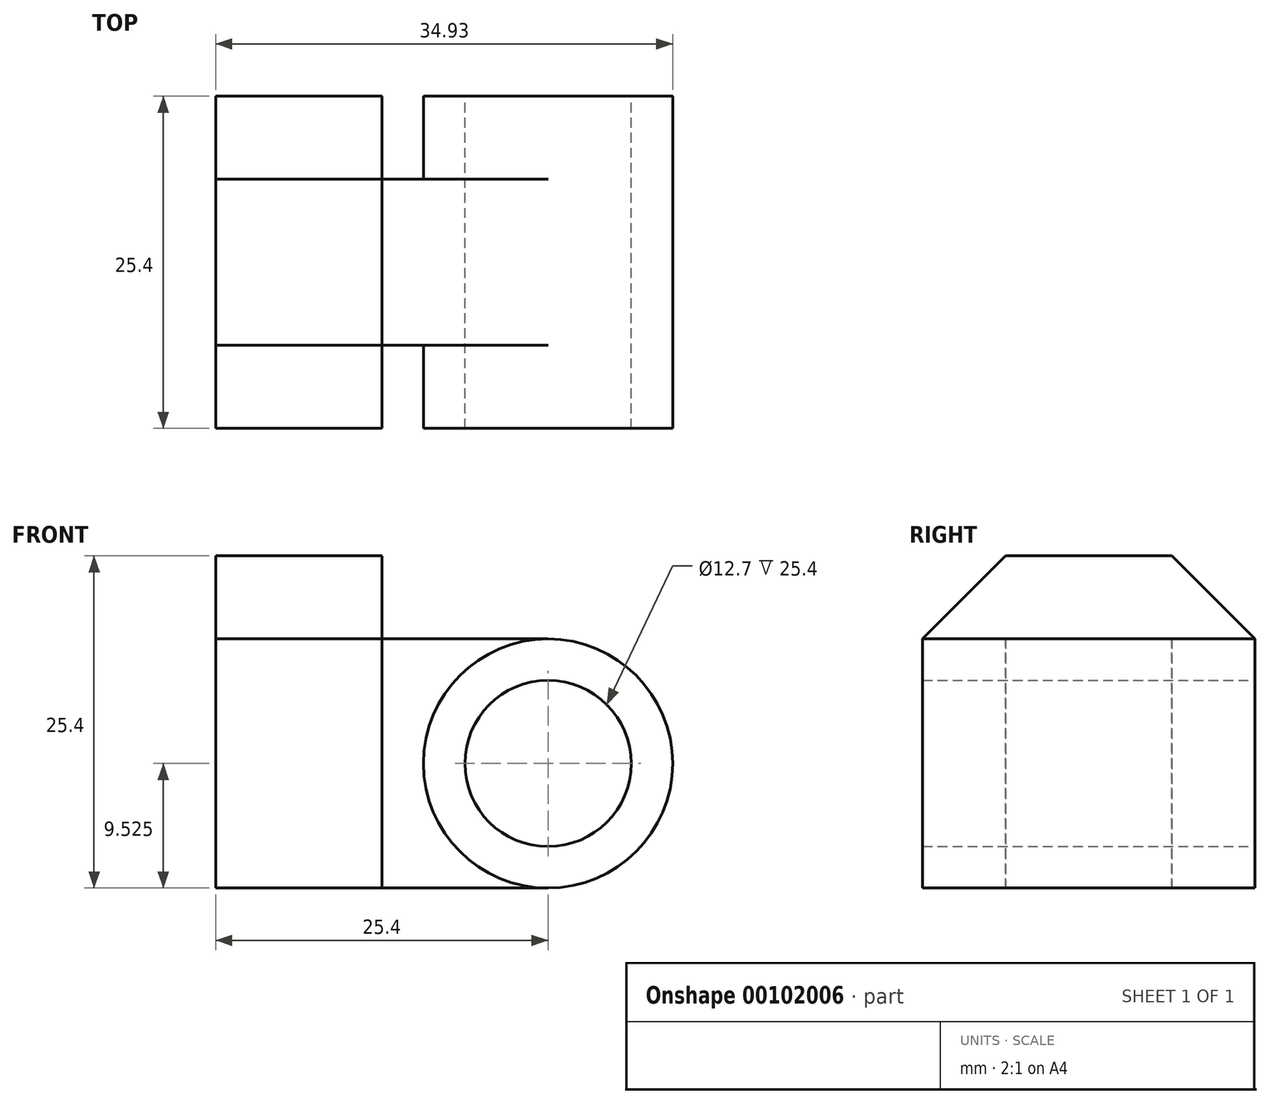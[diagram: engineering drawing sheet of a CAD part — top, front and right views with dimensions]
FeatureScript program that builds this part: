
annotation { "Feature Type Name" : "Feature", "Feature Type Description" : "" }
export const myFeature = defineFeature(function(context is Context, id is Id, definition is map)
    precondition{}
    {
        {
            var Q0;
            Q0=qCreatedBy(makeId("Front.planeOp"),FACE);
            var sketch = newSketch(context, id + "F0", { "sketchPlane" : qUnion([Q0])});
            skLineSegment(sketch, "E0", {"start": v(0, 0) * mm, "end": v(12.7, 0) * mm});
            skLineSegment(sketch, "E1", {"start": v(12.7, 0) * mm, "end": v(12.7, 25.4) * mm});
            skLineSegment(sketch, "E2", {"start": v(12.7, 25.4) * mm, "end": v(0, 25.4) * mm});
            skLineSegment(sketch, "E3", {"start": v(0, 25.4) * mm, "end": v(0, 0) * mm});
            skLineSegment(sketch, "E4", {"start": v(12.7, 0) * mm, "end": v(25.4, 0) * mm, "construction": true});
            skLineSegment(sketch, "E5", {"start": v(25.4, 0) * mm, "end": v(25.4, 19.05) * mm, "construction": true});
            skCircle(sketch, "E6", {"center": v(25.4, 9.53) * mm, "radius": 9.53 * mm});
            skCircle(sketch, "E7", {"center": v(25.4, 9.53) * mm, "radius": 6.35 * mm});
            skSolve(sketch);
        }
        {
            var Q0;
            Q0 = qSketchRegion(id + "F0", true);
            extrude(context, id + "F1", {"entities" : qUnion([Q0]), "endBound" : BoundingType.SYMMETRIC, "depth" : 25.4 * mm});
        }
        {
            var Q0;
            Q0=qCreatedBy(makeId("Right.planeOp"),FACE);
            var sketch = newSketch(context, id + "F2", { "sketchPlane" : qUnion([Q0])});
            skLineSegment(sketch, "E8", {"start": v(0, 0) * mm, "end": v(6.35, 0) * mm});
            skLineSegment(sketch, "E9", {"start": v(6.35, 0) * mm, "end": v(6.35, 19.05) * mm});
            skLineSegment(sketch, "E10", {"start": v(6.35, 19.05) * mm, "end": v(-6.35, 19.05) * mm});
            skLineSegment(sketch, "E11", {"start": v(-6.35, 19.05) * mm, "end": v(-6.35, 0) * mm});
            skLineSegment(sketch, "E12", {"start": v(-6.35, 0) * mm, "end": v(0, 0) * mm});
            skSolve(sketch);
        }
        {
            var Q0;
            Q0 = qSketchRegion(id + "F2", true);
            var Q1;
            Q1=makeQuery(id+"F1.opExtrude","SWEPT_FACE",FACE,{"disambiguationData":[OSD([sQuery(id+"F0.wireOp",EDGE,"E6")])]});
            extrude(context, id + "F3", {"entities" : qUnion([Q0]), "operationType" : NewBodyOperationType.ADD, "endBound" : BoundingType.UP_TO_SURFACE, "endBoundEntityFace" : qUnion([Q1]), "depth" : 25.4 * mm});
        }
        {
            var Q0;
            Q0=qCreatedBy(makeId("Right.planeOp"),FACE);
            var sketch = newSketch(context, id + "F4", { "sketchPlane" : qUnion([Q0])});
            skLineSegment(sketch, "E13", {"start": v(6.35, 25.4) * mm, "end": v(12.7, 25.4) * mm});
            skLineSegment(sketch, "E14", {"start": v(12.7, 25.4) * mm, "end": v(12.7, 19.05) * mm});
            skLineSegment(sketch, "E15", {"start": v(12.7, 19.05) * mm, "end": v(6.35, 25.4) * mm});
            skLineSegment(sketch, "E16", {"start": v(-6.35, 25.4) * mm, "end": v(-12.7, 25.4) * mm});
            skLineSegment(sketch, "E17", {"start": v(-12.7, 25.4) * mm, "end": v(-12.7, 19.05) * mm});
            skLineSegment(sketch, "E18", {"start": v(-12.7, 19.05) * mm, "end": v(-6.35, 25.4) * mm});
            skSolve(sketch);
        }
        {
            var Q0;
            Q0 = qSketchRegion(id + "F4", true);
            extrude(context, id + "F5", {"entities" : qUnion([Q0]), "operationType" : NewBodyOperationType.REMOVE, "depth" : 12.7 * mm});
        }
    });
